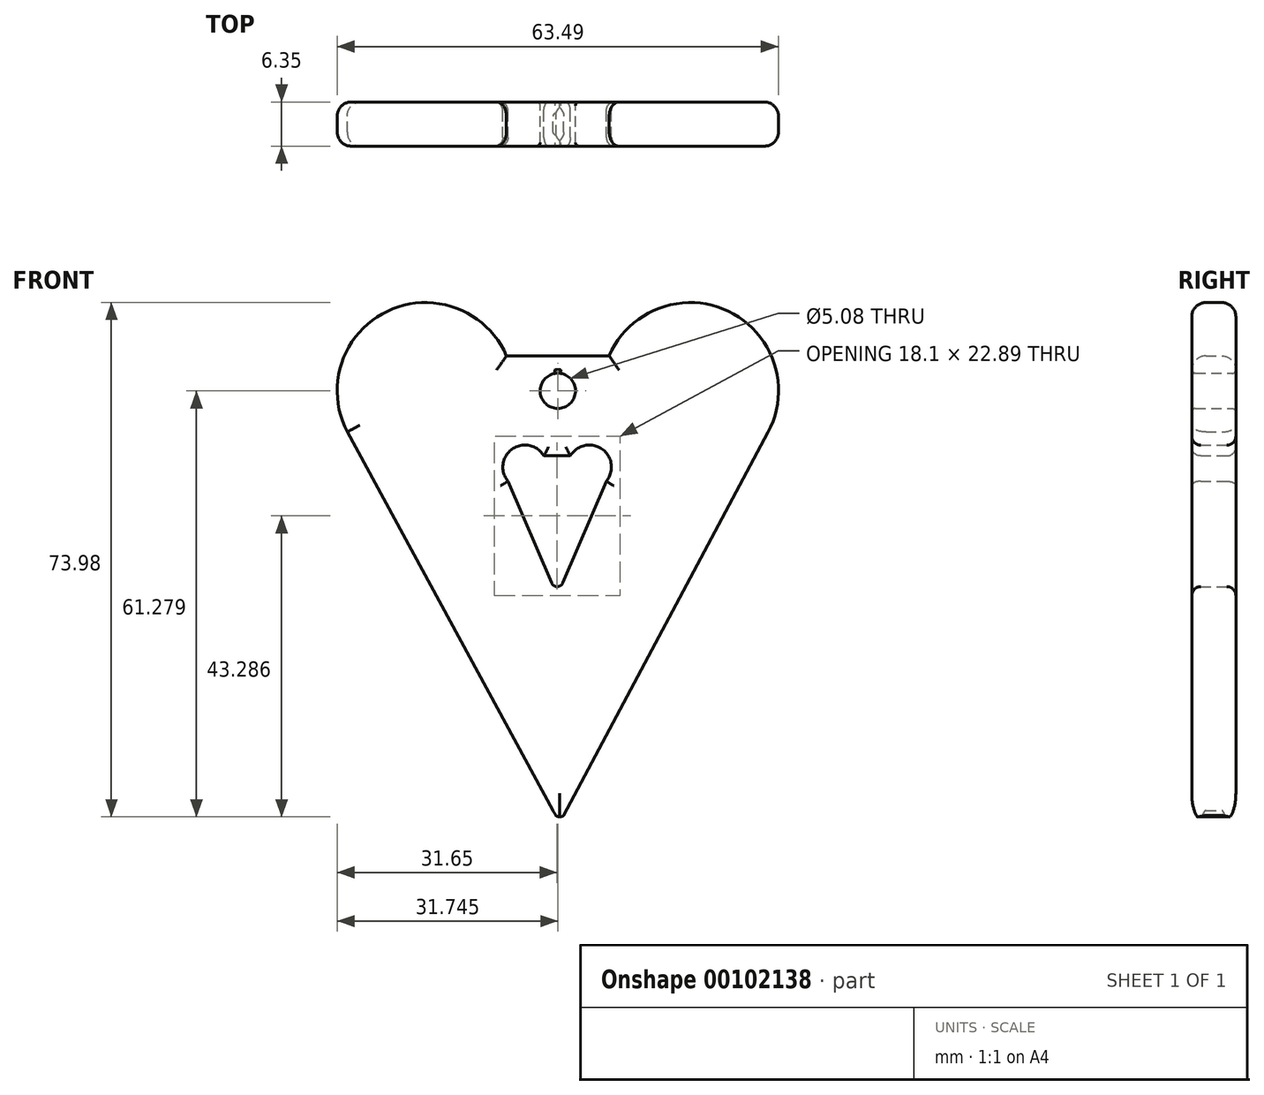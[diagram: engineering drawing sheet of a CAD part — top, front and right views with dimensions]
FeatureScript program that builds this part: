
annotation { "Feature Type Name" : "Feature", "Feature Type Description" : "" }
export const myFeature = defineFeature(function(context is Context, id is Id, definition is map)
    precondition{}
    {
        {
            var Q0;
            Q0=qCreatedBy(makeId("Front.planeOp"),FACE);
            var sketch = newSketch(context, id + "F0", { "sketchPlane" : qUnion([Q0])});
            skArc(sketch, "E0", {"start": v(-32.4, 14.4) * mm, "mid": v(-49.53, 20.8) * mm, "end": v(-55.28, 3.44) * mm});
            skArc(sketch, "E1", {"start": v(5.26, 3.37) * mm, "mid": v(-0.43, 20.79) * mm, "end": v(-17.6, 14.4) * mm});
            skPoint(sketch, "E2.centerSnap0", {"position": v(-25, 9.35) * mm});
            skLineSegment(sketch, "E3", {"start": v(-18.65, -41.45) * mm, "end": v(5.3, 3.44) * mm});
            skLineSegment(sketch, "E4", {"start": v(-32.4, 14.4) * mm, "end": v(-17.6, 14.4) * mm});
            skPoint(sketch, "E5.endSnap0", {"position": v(-24.65, -47.79) * mm});
            skArc(sketch, "E6", {"start": v(-25.24, -51.79) * mm, "mid": v(-24.68, -51.93) * mm, "end": v(-24.13, -51.74) * mm});
            skLineSegment(sketch, "E7.trimOffspring", {"start": v(-23.72, -50.97) * mm, "end": v(-24.13, -51.74) * mm});
            skLineSegment(sketch, "E8.trimOffspring", {"start": v(-25.72, -51.02) * mm, "end": v(-25.24, -51.79) * mm});
            skPoint(sketch, "E2.center.orphan", {"position": v(-25, -41.45) * mm});
            skLineSegment(sketch, "E9", {"start": v(-18.65, -41.45) * mm, "end": v(-23.72, -50.97) * mm});
            skLineSegment(sketch, "E10", {"start": v(-55.28, 3.44) * mm, "end": v(-25.72, -51.02) * mm});
            skCircle(sketch, "E11", {"center": v(-25, 9.35) * mm, "radius": 2.54 * mm});
            skLineSegment(sketch, "E12", {"start": v(-25, 9.35) * mm, "end": v(-25, 0) * mm});
            skArc(sketch, "E13", {"start": v(-27, 0) * mm, "mid": v(-31.56, 0.97) * mm, "end": v(-32.17, -3.65) * mm});
            skArc(sketch, "E14", {"start": v(-18, -3.65) * mm, "mid": v(-18.62, 0.97) * mm, "end": v(-23.18, 0) * mm});
            skLineSegment(sketch, "E15", {"start": v(-27, 0) * mm, "end": v(-23.18, 0) * mm});
            skArc(sketch, "E16", {"start": v(-25.9, -18.29) * mm, "mid": v(-25.09, -18.82) * mm, "end": v(-24.28, -18.29) * mm});
            skPoint(sketch, "E16.centerSnap0", {"position": v(-25.09, -1.62) * mm});
            skLineSegment(sketch, "E17", {"start": v(-32.17, -3.65) * mm, "end": v(-25.9, -18.29) * mm});
            skLineSegment(sketch, "E18", {"start": v(-18, -3.65) * mm, "end": v(-24.28, -18.29) * mm});
            skSolve(sketch);
        }
        {
            var Q0;
            Q0=makeQuery(id+"F0.imprint","IMPRINT",FACE,{"disambiguationData":[TD([[makeQuery(id+"F0.imprint","IMPRINT",EDGE,{"derivedFrom":sQuery(id+"F0.wireOp",EDGE,"E0")}),1.0]])]});
            extrude(context, id + "F1", {"entities" : qUnion([Q0]), "depth" : 6.35 * mm});
        }
        {
            var Q0;
            Q0=makeQuery(id+"F1.opExtrude","CAP_EDGE",EDGE,{"disambiguationData":[OSD([sQuery(id+"F0.wireOp",EDGE,"E0")])],"isStart":false});
            var Q1;
            Q1=makeQuery(id+"F1.opExtrude","CAP_EDGE",EDGE,{"disambiguationData":[OSD([sQuery(id+"F0.wireOp",EDGE,"E10")])],"isStart":false});
            var Q2;
            Q2=makeQuery(id+"F1.opExtrude","CAP_EDGE",EDGE,{"disambiguationData":[OSD([sQuery(id+"F0.wireOp",EDGE,"E1")])],"isStart":false});
            var Q3;
            Q3=makeQuery(id+"F1.opExtrude","CAP_EDGE",EDGE,{"disambiguationData":[OSD([sQuery(id+"F0.wireOp",EDGE,"E4")])],"isStart":false});
            var Q4;
            Q4=makeQuery(id+"F1.opExtrude","CAP_EDGE",EDGE,{"disambiguationData":[OSD([sQuery(id+"F0.wireOp",EDGE,"E0")])],"isStart":true});
            var Q5;
            Q5=makeQuery(id+"F1.opExtrude","CAP_EDGE",EDGE,{"disambiguationData":[OSD([sQuery(id+"F0.wireOp",EDGE,"E10")])],"isStart":true});
            var Q6;
            Q6=makeQuery(id+"F1.opExtrude","CAP_EDGE",EDGE,{"disambiguationData":[OSD([sQuery(id+"F0.wireOp",EDGE,"E4")])],"isStart":true});
            var Q7;
            Q7=makeQuery(id+"F1.opExtrude","CAP_EDGE",EDGE,{"disambiguationData":[OSD([sQuery(id+"F0.wireOp",EDGE,"E1")])],"isStart":true});
            fillet(context, id + "F2", {"entities" : qUnion([Q0, Q1, Q2, Q3, Q4, Q5, Q6, Q7]), "radius" : 2.03 * mm, "tangentPropagation" : true, "allowEdgeOverflow" : false});
        }
        {
            var Q0;
            Q0=makeQuery(id+"F1.opExtrude","CAP_EDGE",EDGE,{"disambiguationData":[OSD([sQuery(id+"F0.wireOp",EDGE,"E11")])],"isStart":false});
            var Q1;
            Q1=makeQuery(id+"F1.opExtrude","CAP_EDGE",EDGE,{"disambiguationData":[OSD([sQuery(id+"F0.wireOp",EDGE,"E11")])],"isStart":true});
            fillet(context, id + "F3", {"entities" : qUnion([Q0, Q1]), "radius" : 0.5 * mm, "tangentPropagation" : true, "allowEdgeOverflow" : false});
        }
        {
            var Q0;
            Q0=makeQuery(id+"F1.opExtrude","CAP_EDGE",EDGE,{"disambiguationData":[OSD([sQuery(id+"F0.wireOp",EDGE,"E13")])],"isStart":false});
            var Q1;
            Q1=makeQuery(id+"F1.opExtrude","CAP_FACE",FACE,{"disambiguationData":[OSD([sQuery(id+"F0.wireOp",EDGE,"E0"),sQuery(id+"F0.wireOp",EDGE,"E1"),sQuery(id+"F0.wireOp",EDGE,"E3"),sQuery(id+"F0.wireOp",EDGE,"E4"),sQuery(id+"F0.wireOp",EDGE,"E6"),sQuery(id+"F0.wireOp",EDGE,"E7.trimOffspring"),sQuery(id+"F0.wireOp",EDGE,"E8.trimOffspring"),sQuery(id+"F0.wireOp",EDGE,"E9"),sQuery(id+"F0.wireOp",EDGE,"E10"),sQuery(id+"F0.wireOp",EDGE,"E11"),sQuery(id+"F0.wireOp",EDGE,"E13"),sQuery(id+"F0.wireOp",EDGE,"E14"),sQuery(id+"F0.wireOp",EDGE,"E15"),sQuery(id+"F0.wireOp",EDGE,"E16"),sQuery(id+"F0.wireOp",EDGE,"E17"),sQuery(id+"F0.wireOp",EDGE,"E18")])],"isStart":false});
            var Q2;
            Q2=makeQuery(id+"F1.opExtrude","CAP_EDGE",EDGE,{"disambiguationData":[OSD([sQuery(id+"F0.wireOp",EDGE,"E17")])],"isStart":false});
            var Q3;
            Q3=makeQuery(id+"F1.opExtrude","CAP_EDGE",EDGE,{"disambiguationData":[OSD([sQuery(id+"F0.wireOp",EDGE,"E16")])],"isStart":false});
            var Q4;
            Q4=makeQuery(id+"F1.opExtrude","CAP_EDGE",EDGE,{"disambiguationData":[OSD([sQuery(id+"F0.wireOp",EDGE,"E18")])],"isStart":false});
            var Q5;
            Q5=makeQuery(id+"F1.opExtrude","CAP_EDGE",EDGE,{"disambiguationData":[OSD([sQuery(id+"F0.wireOp",EDGE,"E14")])],"isStart":false});
            var Q6;
            Q6=makeQuery(id+"F1.opExtrude","CAP_EDGE",EDGE,{"disambiguationData":[OSD([sQuery(id+"F0.wireOp",EDGE,"E15")])],"isStart":false});
            var Q7;
            Q7=makeQuery(id+"F1.opExtrude","CAP_EDGE",EDGE,{"disambiguationData":[OSD([sQuery(id+"F0.wireOp",EDGE,"E18")])],"isStart":true});
            var Q8;
            Q8=makeQuery(id+"F1.opExtrude","CAP_EDGE",EDGE,{"disambiguationData":[OSD([sQuery(id+"F0.wireOp",EDGE,"E16")])],"isStart":true});
            var Q9;
            Q9=makeQuery(id+"F1.opExtrude","CAP_EDGE",EDGE,{"disambiguationData":[OSD([sQuery(id+"F0.wireOp",EDGE,"E17")])],"isStart":true});
            var Q10;
            Q10=makeQuery(id+"F1.opExtrude","CAP_EDGE",EDGE,{"disambiguationData":[OSD([sQuery(id+"F0.wireOp",EDGE,"E13")])],"isStart":true});
            var Q11;
            Q11=makeQuery(id+"F1.opExtrude","CAP_EDGE",EDGE,{"disambiguationData":[OSD([sQuery(id+"F0.wireOp",EDGE,"E15")])],"isStart":true});
            var Q12;
            Q12=makeQuery(id+"F1.opExtrude","CAP_EDGE",EDGE,{"disambiguationData":[OSD([sQuery(id+"F0.wireOp",EDGE,"E14")])],"isStart":true});
            fillet(context, id + "F4", {"entities" : qUnion([Q0, Q1, Q2, Q3, Q4, Q5, Q6, Q7, Q8, Q9, Q10, Q11, Q12]), "radius" : 1.27 * mm, "tangentPropagation" : true, "allowEdgeOverflow" : false});
        }
    });
